# Revit family: Water_Heaters_HAJDU_AQUASTIC-AQ-ECO-ErP_
name_source: partatom
category: Mechanical Equipment
units: mm (PartAtom-declared; Revit-internal decimal feet)

## family parameters
Classification = None
Cut with Voids When Loaded = No
Host = Face
Maintain Annotation Orientation = No
OmniClass Number = 23.31.29.13
OmniClass Title = Hot Water Tank Heaters
Part Type = Normal
Room Calculation Point = No
Round Connector Dimension = Use Diameter
Shared = No

## types (1)
- Nem típus - Terheléstípus katalógus!
    A melegvíz maximális homérséklete = 80 °C
    Csapolási profil = S
    Csatlakozás leírása = Elektromos csatlakozó
    Csatlakozó eltolás = 540 mm  [stored 1.77165 ft]
    Default Elevation = 1219 mm
    Description = Az elektromos, zártrendszerű forróvíztárolók a használati melegvíz igény kielégítésére szolgálnak. A zártrendszerű tárolós vízmelegítők tartálya acéllemezből készül, a korrózió elleni védelmet speciális, titán tartalmú tűzzománc bevonat és aktív magnézium anód biztosítja. Ezek a készülékek több vízvételi hely, illetve zuhanyzós csaptelepek ellátására alkalmasak. A készülékek hőszigetelése freonmentes,  poliuretán szigetelő hab. A fémburkolatú kivitelek nanokerámiás felület előkészítéssel rendelkeznek.
    Dimenzió "a" = 343 mm  [stored 1.12533 ft]
    Energiahatékonysági osztály = С
    Felfutési ido 15°C-ról 65°C-ra = 1 h
    Feszültség = 230 V
    Frekvencia = 50 Hz
    Futobetét típusa = csőfűtőtest
    Futoteljesítmény = 1800 W
    Fázisok száma = 1
    Házház anyaga = Hajdu - Felület - Fehér
    Látszólagos terhelés = 2300 VA
    Magasság = 540 mm  [stored 1.77165 ft]
    Manufacturer = HAJDU
    Model = Modell nincs megadva - Terheléstípus katalógus!
    Névleges urtartalom = 30 l
    Névleges üzemi nyomás = 0.6 MPa
    Product Page URL = https://hajdurt.hu
    Rendeltetés = Zártrendszerű forróvíztároló
    Teljesítménytényezo = 1
    Tömeg = 16.20 kg
    URL = https://hajdurt.hu
    Védettségi fokozat = IPX4
    Vízcsatlakozás = 13 mm
    Z30 = Yes
    Áramfelvétel = 10 A
    Átméro = 410 mm  [stored 1.34514 ft]
    Érintésvédelmi osztály = I.

note: [stored X ft] marks values corroborated as IEEE doubles in the binary element streams (Revit-internal decimal feet)

## geometry (parser evidence)
native form markers: Sweep x6
no freeform markers — native parametric forms only
